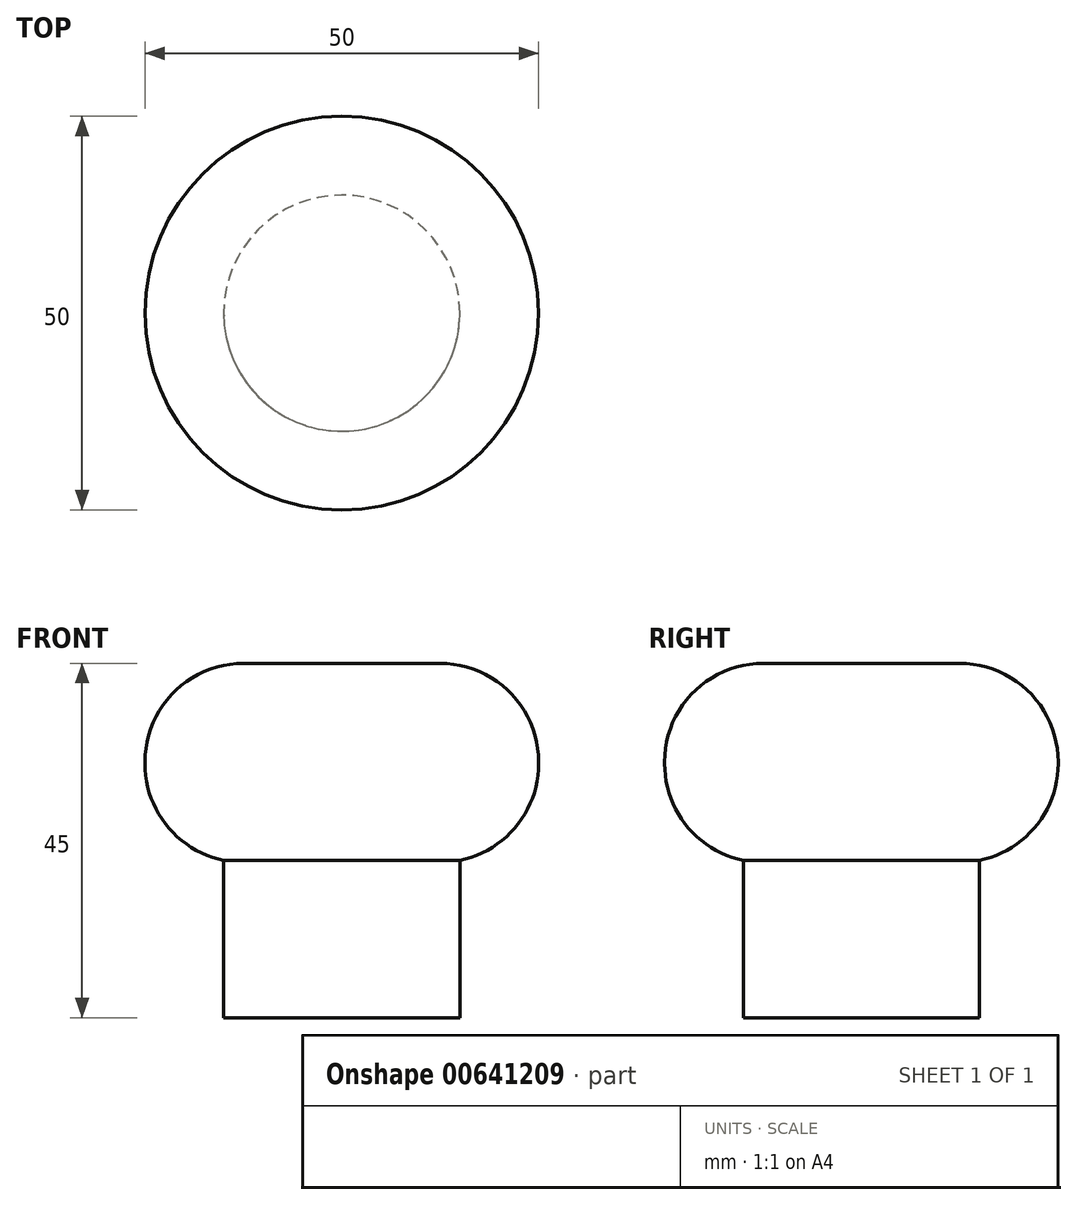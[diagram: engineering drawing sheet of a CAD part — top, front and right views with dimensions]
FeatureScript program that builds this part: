
annotation { "Feature Type Name" : "Feature", "Feature Type Description" : "" }
export const myFeature = defineFeature(function(context is Context, id is Id, definition is map)
    precondition{}
    {
        {
            var Q0;
            Q0=qCreatedBy(makeId("Top.planeOp"),FACE);
            var sketch = newSketch(context, id + "F0", { "sketchPlane" : qUnion([Q0])});
            skCircle(sketch, "E0", {"center": v(0, 0) * mm, "radius": 15 * mm});
            skSolve(sketch);
        }
        {
            var Q0;
            Q0 = qSketchRegion(id + "F0", true);
            extrude(context, id + "F1", {"entities" : qUnion([Q0]), "depth" : 20 * mm, "offsetDistance" : 25 * mm});
        }
        {
            var Q0;
            Q0=makeQuery(id+"F1.opExtrude","CAP_FACE",FACE,{"disambiguationData":[OSD([sQuery(id+"F0.wireOp",EDGE,"E0")])],"isStart":false});
            var sketch = newSketch(context, id + "F2", { "sketchPlane" : qUnion([Q0])});
            skCircle(sketch, "E1", {"center": v(0, 0) * mm, "radius": 25 * mm});
            skSolve(sketch);
        }
        {
            var Q0;
            Q0 = qSketchRegion(id + "F2", true);
            extrude(context, id + "F3", {"entities" : qUnion([Q0]), "operationType" : NewBodyOperationType.ADD, "depth" : 25 * mm, "offsetDistance" : 25 * mm});
        }
        {
            var Q0;
            Q0=makeQuery(id+"F3.opExtrude","CAP_EDGE",EDGE,{"disambiguationData":[OSD([sQuery(id+"F2.wireOp",EDGE,"E1")])],"isStart":false});
            var Q1;
            Q1=makeQuery(id+"F3.opExtrude","CAP_EDGE",EDGE,{"disambiguationData":[OSD([sQuery(id+"F2.wireOp",EDGE,"E1")])],"isStart":true});
            fillet(context, id + "F4", {"entities" : qUnion([Q0, Q1]), "radius" : 12.5 * mm, "tangentPropagation" : true, "allowEdgeOverflow" : false});
        }
    });
